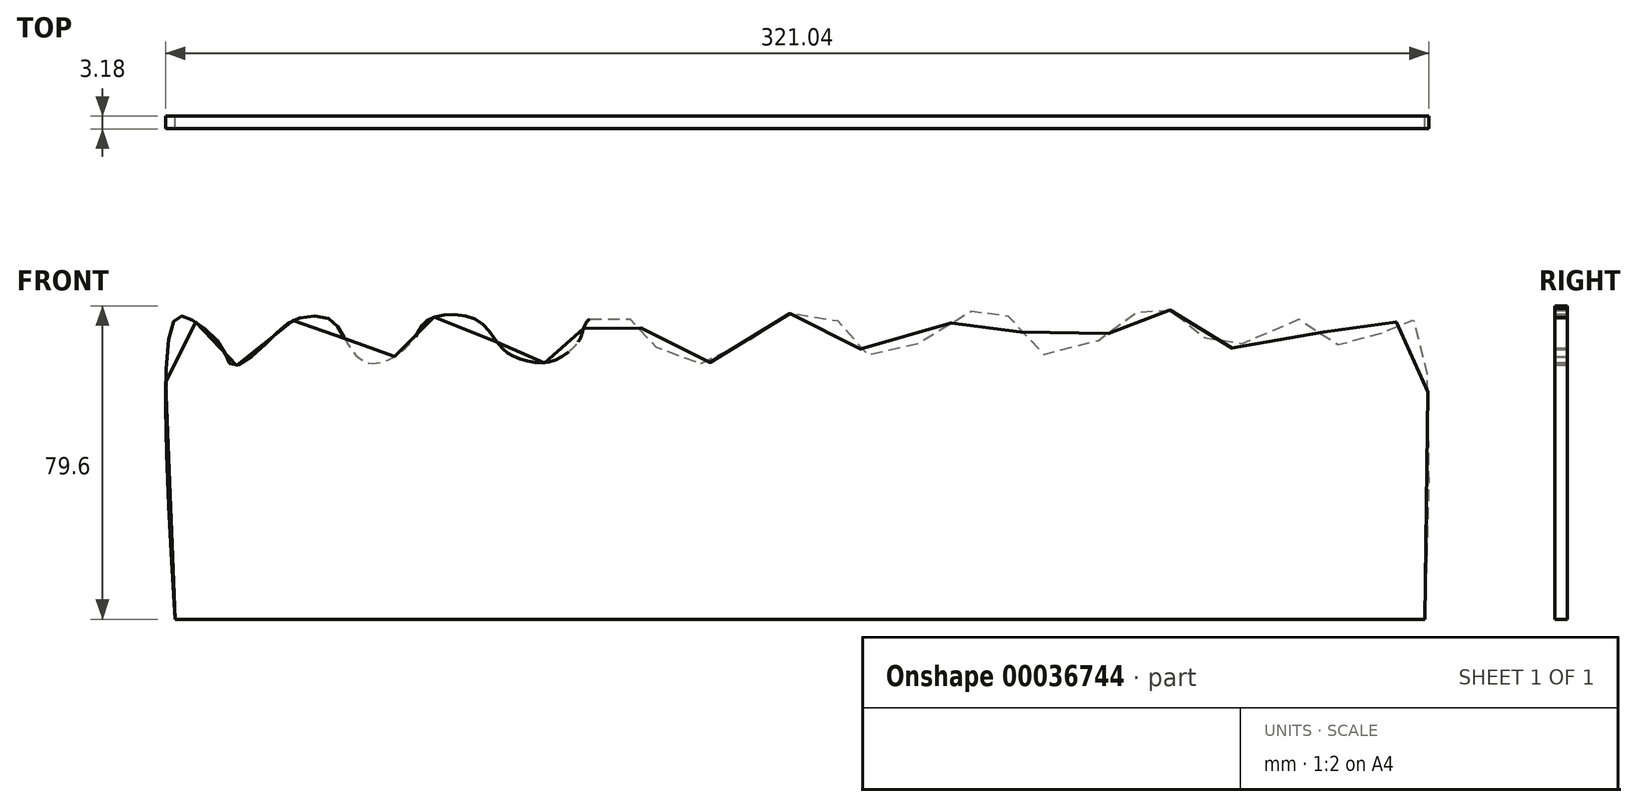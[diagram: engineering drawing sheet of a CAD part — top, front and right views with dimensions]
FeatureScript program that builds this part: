
annotation { "Feature Type Name" : "Feature", "Feature Type Description" : "" }
export const myFeature = defineFeature(function(context is Context, id is Id, definition is map)
    precondition{}
    {
        {
            var Q0;
            Q0=qCreatedBy(makeId("Front.planeOp"),FACE);
            var sketch = newSketch(context, id + "F0", { "sketchPlane" : qUnion([Q0])});
            skLineSegment(sketch, "E0", {"start": v(-158.88, -9.6) * mm, "end": v(158.62, -9.6) * mm, "construction": true});
            skLineSegment(sketch, "E1", {"start": v(-158.88, -9.6) * mm, "end": v(-158.88, 66.6) * mm, "construction": true});
            skLineSegment(sketch, "E2", {"start": v(158.62, -9.6) * mm, "end": v(158.62, 66.6) * mm, "construction": true});
            skLineSegment(sketch, "E3", {"start": v(-158.88, -9.6) * mm, "end": v(158.62, -9.6) * mm});
            skFitSpline(sketch, "E4", {"points": [v(-158.88, -9.6) * mm, v(-158.88, 66.6) * mm, v(-154.92, 66.6) * mm, v(-146.77, 59.16) * mm, v(-144.2, 54.85) * mm, v(-135.25, 60.92) * mm, v(-128.37, 66.6) * mm, v(-119.58, 66.6) * mm, v(-115.58, 61.24) * mm, v(-110.14, 55.65) * mm, v(-102.79, 57.4) * mm, v(-97.5, 62.68) * mm, v(-94.31, 66.6) * mm, v(-82.64, 66.6) * mm, v(-76.72, 60.28) * mm, v(-72.88, 57.24) * mm, v(-66.16, 55.49) * mm, v(-60.73, 57.08) * mm, v(-55.93, 61.88) * mm, v(-53.7, 66.6) * mm, v(-43.14, 66.6) * mm, v(-36.26, 59.16) * mm, v(-21.55, 55.97) * mm, v(-6.35, 66.6) * mm, v(9, 66.6) * mm, v(18.27, 57.08) * mm, v(39.7, 66.6) * mm, v(50.9, 69.08) * mm, v(63.21, 57.24) * mm, v(82.88, 66.6) * mm, v(87.84, 69.24) * mm, v(98.87, 66.6) * mm, v(106.87, 58.84) * mm, v(127.34, 66.6) * mm, v(139.01, 59.16) * mm, v(152.45, 66.6) * mm, v(156.77, 65.08) * mm, v(158.62, -9.6) * mm], "startDerivative": vector(-95.06, 1564.46) * mm, "endDerivative": vector(-50.56, -1485.74) * mm});
            skSolve(sketch);
        }
        {
            var Q0;
            Q0=makeQuery(id+"F0.imprint","IMPRINT",FACE,{"disambiguationData":[TD([[makeQuery(id+"F0.imprint","IMPRINT",EDGE,{"derivedFrom":sQuery(id+"F0.wireOp",EDGE,"E3")}),1.0]])]});
            extrude(context, id + "F1", {"entities" : qUnion([Q0]), "depth" : 3.17 * mm});
        }
    });
